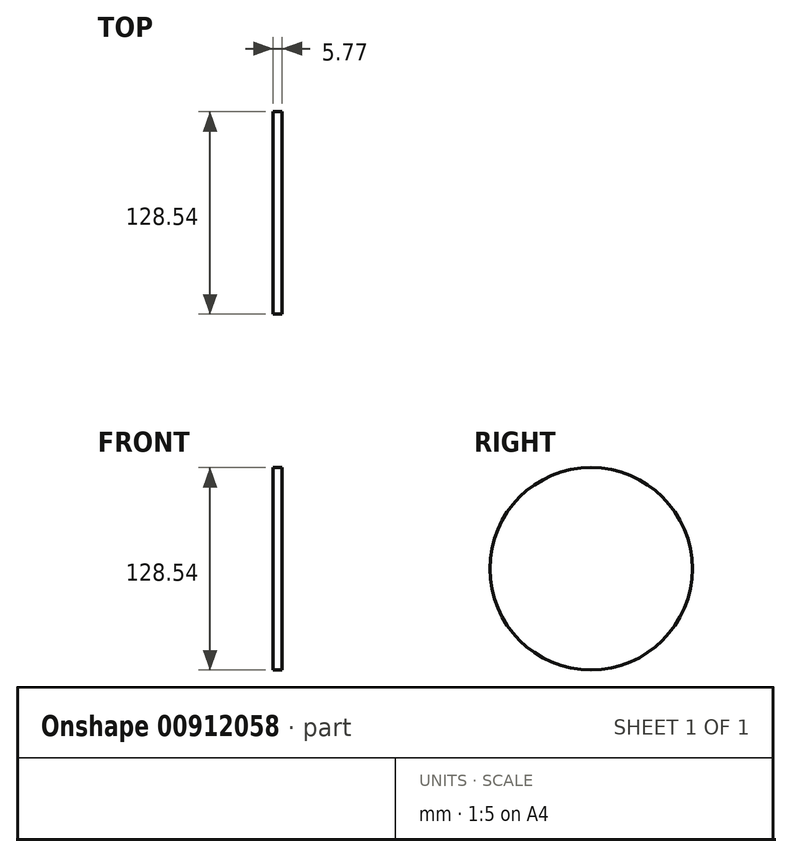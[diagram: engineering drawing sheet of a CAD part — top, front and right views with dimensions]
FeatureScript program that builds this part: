
annotation { "Feature Type Name" : "Feature", "Feature Type Description" : "" }
export const myFeature = defineFeature(function(context is Context, id is Id, definition is map)
    precondition{}
    {
        {
            var Q0;
            Q0=qCreatedBy(makeId("Right.planeOp"),FACE);
            var sketch = newSketch(context, id + "F0", { "sketchPlane" : qUnion([Q0])});
            skLineSegment(sketch, "E0", {"start": v(-7.94, 136.28) * mm, "end": v(-7.94, 136.29) * mm});
            skLineSegment(sketch, "E1.MirrorCS", {"start": v(-7.94, 136.28) * mm, "end": v(-7.94, 136.52) * mm});
            skArc(sketch, "E2.trimOffspring", {"start": v(2.18, 146.92) * mm, "mid": v(-1.44, 143.95) * mm, "end": v(-3.67, 139.84) * mm});
            skPoint(sketch, "E3.start.orphan", {"position": v(0, 68.26) * mm});
            skArc(sketch, "E4.MirrorCS", {"start": v(2.18, 146.92) * mm, "mid": v(5.85, 143.85) * mm, "end": v(8.05, 139.6) * mm});
            skArc(sketch, "E5.MirrorCS", {"start": v(12.63, 135.93) * mm, "mid": v(12.47, 135.94) * mm, "end": v(12.3, 135.96) * mm});
            skArc(sketch, "E6.1.0", {"start": v(-14.9, 146.18) * mm, "mid": v(-10.9, 143.55) * mm, "end": v(-8.21, 139.59) * mm});
            skArc(sketch, "E6.1.1", {"start": v(-14.9, 146.18) * mm, "mid": v(-18.14, 142.81) * mm, "end": v(-19.88, 138.47) * mm});
            skArc(sketch, "E6.1.2", {"start": v(-21.7, 135.42) * mm, "mid": v(-20.52, 136.78) * mm, "end": v(-19.88, 138.47) * mm});
            skArc(sketch, "E6.2.0", {"start": v(-31.76, 143.46) * mm, "mid": v(-27.48, 141.32) * mm, "end": v(-24.36, 137.7) * mm});
            skArc(sketch, "E6.2.1", {"start": v(-31.76, 143.46) * mm, "mid": v(-34.6, 139.74) * mm, "end": v(-35.82, 135.23) * mm});
            skArc(sketch, "E6.2.2", {"start": v(-37.28, 131.99) * mm, "mid": v(-36.26, 133.48) * mm, "end": v(-35.82, 135.23) * mm});
            skArc(sketch, "E6.3.0", {"start": v(-48.2, 138.8) * mm, "mid": v(-43.7, 137.17) * mm, "end": v(-40.18, 133.93) * mm});
            skArc(sketch, "E6.3.1", {"start": v(-48.2, 138.8) * mm, "mid": v(-50.59, 134.78) * mm, "end": v(-51.28, 130.16) * mm});
            skArc(sketch, "E6.3.2", {"start": v(-52.35, 126.77) * mm, "mid": v(-51.5, 128.36) * mm, "end": v(-51.28, 130.16) * mm});
            skArc(sketch, "E6.4.0", {"start": v(-64, 132.27) * mm, "mid": v(-59.33, 131.17) * mm, "end": v(-55.46, 128.36) * mm});
            skArc(sketch, "E6.4.1", {"start": v(-64, 132.27) * mm, "mid": v(-65.9, 128) * mm, "end": v(-66.04, 123.32) * mm});
            skArc(sketch, "E6.4.2", {"start": v(-68.5, 118.08) * mm, "mid": v(-68.43, 118.12) * mm, "end": v(-68.37, 118.16) * mm});
            skArc(sketch, "E6.5.0", {"start": v(-78.91, 123.94) * mm, "mid": v(-74.16, 123.4) * mm, "end": v(-69.99, 121.06) * mm});
            skArc(sketch, "E6.5.1", {"start": v(-78.91, 123.94) * mm, "mid": v(-80.3, 119.48) * mm, "end": v(-79.91, 114.82) * mm});
            skArc(sketch, "E6.5.2", {"start": v(-80.17, 111.28) * mm, "mid": v(-79.72, 113.02) * mm, "end": v(-79.91, 114.82) * mm});
            skArc(sketch, "E6.5.3", {"start": v(-66.71, 119.83) * mm, "mid": v(-68.46, 120.15) * mm, "end": v(-69.99, 121.06) * mm});
            skArc(sketch, "E6.6.0", {"start": v(-92.77, 113.94) * mm, "mid": v(-87.98, 113.95) * mm, "end": v(-83.57, 112.11) * mm});
            skArc(sketch, "E6.6.1", {"start": v(-92.77, 113.94) * mm, "mid": v(-93.64, 109.35) * mm, "end": v(-92.7, 104.77) * mm});
            skArc(sketch, "E6.6.2", {"start": v(-92.55, 101.22) * mm, "mid": v(-92.3, 103) * mm, "end": v(-92.7, 104.77) * mm});
            skArc(sketch, "E6.6.3", {"start": v(-80.17, 111.28) * mm, "mid": v(-81.94, 111.4) * mm, "end": v(-83.57, 112.11) * mm});
            skArc(sketch, "E6.7.0", {"start": v(-105.37, 102.4) * mm, "mid": v(-100.62, 102.97) * mm, "end": v(-96.02, 101.65) * mm});
            skArc(sketch, "E6.7.1", {"start": v(-105.37, 102.4) * mm, "mid": v(-105.7, 97.74) * mm, "end": v(-104.24, 93.3) * mm});
            skArc(sketch, "E6.7.2", {"start": v(-103.68, 89.79) * mm, "mid": v(-103.64, 91.6) * mm, "end": v(-104.24, 93.3) * mm});
            skArc(sketch, "E6.7.3", {"start": v(-92.55, 101.22) * mm, "mid": v(-94.32, 101.13) * mm, "end": v(-96.02, 101.65) * mm});
            skArc(sketch, "E6.8.0", {"start": v(-116.55, 89.48) * mm, "mid": v(-111.9, 90.6) * mm, "end": v(-107.17, 89.82) * mm});
            skArc(sketch, "E6.8.1", {"start": v(-116.55, 89.48) * mm, "mid": v(-116.33, 84.8) * mm, "end": v(-114.36, 80.57) * mm});
            skArc(sketch, "E6.8.2", {"start": v(-113.4, 77.14) * mm, "mid": v(-113.57, 78.94) * mm, "end": v(-114.36, 80.57) * mm});
            skArc(sketch, "E6.8.3", {"start": v(-103.68, 89.79) * mm, "mid": v(-105.43, 89.5) * mm, "end": v(-107.17, 89.82) * mm});
            skArc(sketch, "E6.9.0", {"start": v(-126.15, 75.34) * mm, "mid": v(-121.65, 76.99) * mm, "end": v(-116.87, 76.77) * mm});
            skArc(sketch, "E6.9.1", {"start": v(-126.15, 75.34) * mm, "mid": v(-125.39, 70.73) * mm, "end": v(-122.94, 66.74) * mm});
            skArc(sketch, "E6.9.2", {"start": v(-121.59, 63.46) * mm, "mid": v(-121.97, 65.22) * mm, "end": v(-122.94, 66.74) * mm});
            skArc(sketch, "E6.9.3", {"start": v(-113.4, 77.14) * mm, "mid": v(-115.1, 76.65) * mm, "end": v(-116.87, 76.77) * mm});
            skArc(sketch, "E6.10.0", {"start": v(-134.04, 60.19) * mm, "mid": v(-129.77, 62.34) * mm, "end": v(-125, 62.68) * mm});
            skArc(sketch, "E6.10.1", {"start": v(-134.04, 60.19) * mm, "mid": v(-132.75, 55.7) * mm, "end": v(-129.86, 52.02) * mm});
            skArc(sketch, "E6.10.2", {"start": v(-128.13, 48.91) * mm, "mid": v(-128.72, 50.62) * mm, "end": v(-129.86, 52.02) * mm});
            skArc(sketch, "E6.10.3", {"start": v(-121.59, 63.46) * mm, "mid": v(-123.22, 62.77) * mm, "end": v(-125, 62.68) * mm});
            skArc(sketch, "E6.11.0", {"start": v(-140.12, 44.22) * mm, "mid": v(-136.13, 46.86) * mm, "end": v(-131.43, 47.75) * mm});
            skArc(sketch, "E6.11.1", {"start": v(-140.12, 44.22) * mm, "mid": v(-138.32, 39.9) * mm, "end": v(-135.02, 36.6) * mm});
            skArc(sketch, "E6.11.2", {"start": v(-132.94, 33.7) * mm, "mid": v(-133.72, 35.34) * mm, "end": v(-135.02, 36.6) * mm});
            skArc(sketch, "E6.11.3", {"start": v(-128.13, 48.91) * mm, "mid": v(-129.68, 48.04) * mm, "end": v(-131.43, 47.75) * mm});
            skArc(sketch, "E6.12.0", {"start": v(-144.3, 27.65) * mm, "mid": v(-140.65, 30.74) * mm, "end": v(-136.08, 32.17) * mm});
            skArc(sketch, "E6.12.1", {"start": v(-144.3, 27.65) * mm, "mid": v(-142.02, 23.58) * mm, "end": v(-138.36, 20.67) * mm});
            skArc(sketch, "E6.12.2", {"start": v(-135.96, 18.04) * mm, "mid": v(-136.92, 19.57) * mm, "end": v(-138.36, 20.67) * mm});
            skArc(sketch, "E6.12.3", {"start": v(-132.94, 33.7) * mm, "mid": v(-134.38, 32.66) * mm, "end": v(-136.08, 32.17) * mm});
            skArc(sketch, "E6.13.0", {"start": v(-146.54, 10.71) * mm, "mid": v(-143.26, 14.2) * mm, "end": v(-138.9, 16.15) * mm});
            skArc(sketch, "E6.13.1", {"start": v(-146.54, 10.71) * mm, "mid": v(-143.8, 6.93) * mm, "end": v(-139.82, 4.47) * mm});
            skArc(sketch, "E6.13.2", {"start": v(-137.13, 2.14) * mm, "mid": v(-138.27, 3.55) * mm, "end": v(-139.82, 4.47) * mm});
            skArc(sketch, "E6.13.3", {"start": v(-135.96, 18.04) * mm, "mid": v(-137.26, 16.84) * mm, "end": v(-138.9, 16.15) * mm});
            skArc(sketch, "E6.14.0", {"start": v(-146.8, -6.37) * mm, "mid": v(-143.94, -2.53) * mm, "end": v(-139.83, -0.08) * mm});
            skArc(sketch, "E6.14.1", {"start": v(-146.8, -6.37) * mm, "mid": v(-143.63, -9.8) * mm, "end": v(-139.4, -11.8) * mm});
            skArc(sketch, "E6.14.2", {"start": v(-136.45, -13.8) * mm, "mid": v(-137.74, -12.53) * mm, "end": v(-139.4, -11.8) * mm});
            skArc(sketch, "E6.14.3", {"start": v(-137.13, 2.14) * mm, "mid": v(-138.28, 0.79) * mm, "end": v(-139.83, -0.08) * mm});
            skArc(sketch, "E6.15.0", {"start": v(-145.06, -23.37) * mm, "mid": v(-142.68, -19.22) * mm, "end": v(-138.88, -16.31) * mm});
            skArc(sketch, "E6.15.1", {"start": v(-145.06, -23.37) * mm, "mid": v(-141.52, -26.42) * mm, "end": v(-137.08, -27.9) * mm});
            skArc(sketch, "E6.15.2", {"start": v(-133.93, -29.54) * mm, "mid": v(-135.36, -28.44) * mm, "end": v(-137.08, -27.9) * mm});
            skArc(sketch, "E6.15.3", {"start": v(-136.45, -13.8) * mm, "mid": v(-137.44, -15.27) * mm, "end": v(-138.88, -16.31) * mm});
            skArc(sketch, "E6.16.0", {"start": v(-141.37, -40.05) * mm, "mid": v(-139.48, -35.65) * mm, "end": v(-136.04, -32.33) * mm});
            skArc(sketch, "E6.16.1", {"start": v(-141.37, -40.05) * mm, "mid": v(-137.5, -42.67) * mm, "end": v(-132.92, -43.62) * mm});
            skArc(sketch, "E6.16.2", {"start": v(-129.6, -44.9) * mm, "mid": v(-131.14, -43.96) * mm, "end": v(-132.92, -43.62) * mm});
            skArc(sketch, "E6.16.3", {"start": v(-133.93, -29.54) * mm, "mid": v(-134.74, -31.12) * mm, "end": v(-136.04, -32.33) * mm});
            skArc(sketch, "E6.17.0", {"start": v(-135.76, -56.2) * mm, "mid": v(-134.4, -51.6) * mm, "end": v(-131.37, -47.9) * mm});
            skArc(sketch, "E6.17.1", {"start": v(-135.76, -56.2) * mm, "mid": v(-131.61, -58.34) * mm, "end": v(-126.95, -58.76) * mm});
            skArc(sketch, "E6.17.2", {"start": v(-123.5, -59.63) * mm, "mid": v(-125.15, -58.89) * mm, "end": v(-126.95, -58.76) * mm});
            skArc(sketch, "E6.17.3", {"start": v(-129.6, -44.9) * mm, "mid": v(-130.22, -46.55) * mm, "end": v(-131.37, -47.9) * mm});
            skArc(sketch, "E6.18.0", {"start": v(-128.32, -71.57) * mm, "mid": v(-127.5, -66.86) * mm, "end": v(-124.92, -62.83) * mm});
            skArc(sketch, "E6.18.1", {"start": v(-128.32, -71.57) * mm, "mid": v(-123.95, -73.23) * mm, "end": v(-119.27, -73.1) * mm});
            skArc(sketch, "E6.18.2", {"start": v(-115.75, -73.57) * mm, "mid": v(-117.47, -73.02) * mm, "end": v(-119.27, -73.1) * mm});
            skArc(sketch, "E6.18.3", {"start": v(-123.5, -59.63) * mm, "mid": v(-123.93, -61.36) * mm, "end": v(-124.92, -62.83) * mm});
            skArc(sketch, "E6.19.0", {"start": v(-119.14, -85.99) * mm, "mid": v(-118.88, -81.2) * mm, "end": v(-116.78, -76.9) * mm});
            skArc(sketch, "E6.19.1", {"start": v(-119.14, -85.99) * mm, "mid": v(-114.6, -87.12) * mm, "end": v(-109.98, -86.45) * mm});
            skArc(sketch, "E6.19.2", {"start": v(-106.43, -86.5) * mm, "mid": v(-108.2, -86.16) * mm, "end": v(-109.98, -86.45) * mm});
            skArc(sketch, "E6.19.3", {"start": v(-115.75, -73.57) * mm, "mid": v(-115.97, -75.33) * mm, "end": v(-116.78, -76.9) * mm});
            skArc(sketch, "E6.20.0", {"start": v(-108.36, -99.24) * mm, "mid": v(-108.64, -94.46) * mm, "end": v(-107.06, -89.94) * mm});
            skArc(sketch, "E6.20.1", {"start": v(-108.36, -99.24) * mm, "mid": v(-103.72, -99.84) * mm, "end": v(-99.2, -98.64) * mm});
            skArc(sketch, "E6.20.2", {"start": v(-95.66, -98.28) * mm, "mid": v(-97.46, -98.14) * mm, "end": v(-99.2, -98.64) * mm});
            skArc(sketch, "E6.20.3", {"start": v(-106.43, -86.5) * mm, "mid": v(-106.44, -88.28) * mm, "end": v(-107.06, -89.94) * mm});
            skArc(sketch, "E6.21.0", {"start": v(-96.1, -111.15) * mm, "mid": v(-96.94, -106.43) * mm, "end": v(-95.9, -101.77) * mm});
            skArc(sketch, "E6.21.1", {"start": v(-96.1, -111.15) * mm, "mid": v(-91.43, -111.2) * mm, "end": v(-87.08, -109.49) * mm});
            skArc(sketch, "E6.21.2", {"start": v(-83.6, -108.72) * mm, "mid": v(-85.41, -108.79) * mm, "end": v(-87.08, -109.49) * mm});
            skArc(sketch, "E6.21.3", {"start": v(-95.66, -98.28) * mm, "mid": v(-95.47, -100.04) * mm, "end": v(-95.9, -101.77) * mm});
            skArc(sketch, "E6.22.0", {"start": v(-82.55, -121.55) * mm, "mid": v(-83.93, -116.97) * mm, "end": v(-83.44, -112.21) * mm});
            skArc(sketch, "E6.22.1", {"start": v(-82.55, -121.55) * mm, "mid": v(-77.9, -121.06) * mm, "end": v(-73.78, -118.86) * mm});
            skArc(sketch, "E6.22.2", {"start": v(-70.42, -117.7) * mm, "mid": v(-72.2, -117.97) * mm, "end": v(-73.78, -118.86) * mm});
            skArc(sketch, "E6.22.3", {"start": v(-83.6, -108.72) * mm, "mid": v(-83.21, -110.45) * mm, "end": v(-83.44, -112.21) * mm});
            skArc(sketch, "E6.23.0", {"start": v(-67.88, -130.31) * mm, "mid": v(-69.78, -125.92) * mm, "end": v(-69.84, -121.14) * mm});
            skArc(sketch, "E6.23.1", {"start": v(-67.88, -130.31) * mm, "mid": v(-63.32, -129.29) * mm, "end": v(-59.48, -126.62) * mm});
            skArc(sketch, "E6.23.2", {"start": v(-56.28, -125.07) * mm, "mid": v(-58.02, -125.55) * mm, "end": v(-59.48, -126.62) * mm});
            skArc(sketch, "E6.23.3", {"start": v(-70.42, -117.7) * mm, "mid": v(-69.83, -119.36) * mm, "end": v(-69.84, -121.14) * mm});
            skArc(sketch, "E6.24.0", {"start": v(-52.3, -137.31) * mm, "mid": v(-54.7, -133.17) * mm, "end": v(-55.3, -128.43) * mm});
            skArc(sketch, "E6.24.1", {"start": v(-52.3, -137.31) * mm, "mid": v(-47.88, -135.77) * mm, "end": v(-44.38, -132.67) * mm});
            skArc(sketch, "E6.24.2", {"start": v(-41.38, -130.76) * mm, "mid": v(-43.05, -131.44) * mm, "end": v(-44.38, -132.67) * mm});
            skArc(sketch, "E6.24.3", {"start": v(-56.28, -125.07) * mm, "mid": v(-55.5, -126.66) * mm, "end": v(-55.3, -128.43) * mm});
            skArc(sketch, "E6.25.0", {"start": v(-36, -142.45) * mm, "mid": v(-38.86, -138.62) * mm, "end": v(-40.03, -133.98) * mm});
            skArc(sketch, "E6.25.1", {"start": v(-36, -142.45) * mm, "mid": v(-31.8, -140.4) * mm, "end": v(-28.68, -136.92) * mm});
            skArc(sketch, "E6.25.2", {"start": v(-25.92, -134.68) * mm, "mid": v(-27.5, -135.55) * mm, "end": v(-28.68, -136.92) * mm});
            skArc(sketch, "E6.25.3", {"start": v(-41.38, -130.76) * mm, "mid": v(-40.42, -132.25) * mm, "end": v(-40.03, -133.98) * mm});
            skArc(sketch, "E6.26.0", {"start": v(-19.22, -145.67) * mm, "mid": v(-22.5, -142.2) * mm, "end": v(-24.2, -137.72) * mm});
            skArc(sketch, "E6.26.1", {"start": v(-19.22, -145.67) * mm, "mid": v(-15.28, -143.15) * mm, "end": v(-12.59, -139.33) * mm});
            skArc(sketch, "E6.26.2", {"start": v(-10.1, -136.78) * mm, "mid": v(-11.58, -137.83) * mm, "end": v(-12.59, -139.33) * mm});
            skArc(sketch, "E6.26.3", {"start": v(-25.92, -134.68) * mm, "mid": v(-24.8, -136.05) * mm, "end": v(-24.2, -137.72) * mm});
            skArc(sketch, "E6.27.0", {"start": v(-2.18, -146.92) * mm, "mid": v(-5.85, -143.85) * mm, "end": v(-8.05, -139.6) * mm});
            skArc(sketch, "E6.27.1", {"start": v(-2.18, -146.92) * mm, "mid": v(1.44, -143.95) * mm, "end": v(3.67, -139.84) * mm});
            skArc(sketch, "E6.27.2", {"start": v(5.84, -137.03) * mm, "mid": v(4.5, -138.24) * mm, "end": v(3.67, -139.84) * mm});
            skArc(sketch, "E6.27.3", {"start": v(-10.1, -136.78) * mm, "mid": v(-8.83, -138) * mm, "end": v(-8.05, -139.6) * mm});
            skArc(sketch, "E6.28.0", {"start": v(14.9, -146.18) * mm, "mid": v(10.9, -143.55) * mm, "end": v(8.21, -139.59) * mm});
            skArc(sketch, "E6.28.1", {"start": v(14.9, -146.18) * mm, "mid": v(18.14, -142.81) * mm, "end": v(19.88, -138.47) * mm});
            skArc(sketch, "E6.28.2", {"start": v(21.7, -135.42) * mm, "mid": v(20.52, -136.78) * mm, "end": v(19.88, -138.47) * mm});
            skArc(sketch, "E6.28.3", {"start": v(5.84, -137.03) * mm, "mid": v(7.25, -138.1) * mm, "end": v(8.21, -139.59) * mm});
            skArc(sketch, "E6.29.0", {"start": v(31.76, -143.46) * mm, "mid": v(27.48, -141.32) * mm, "end": v(24.36, -137.7) * mm});
            skArc(sketch, "E6.29.1", {"start": v(31.76, -143.46) * mm, "mid": v(34.6, -139.74) * mm, "end": v(35.82, -135.23) * mm});
            skArc(sketch, "E6.29.2", {"start": v(37.28, -131.99) * mm, "mid": v(36.26, -133.48) * mm, "end": v(35.82, -135.23) * mm});
            skArc(sketch, "E6.29.3", {"start": v(21.7, -135.42) * mm, "mid": v(23.24, -136.32) * mm, "end": v(24.36, -137.7) * mm});
            skArc(sketch, "E6.30.0", {"start": v(48.2, -138.8) * mm, "mid": v(43.7, -137.17) * mm, "end": v(40.18, -133.93) * mm});
            skArc(sketch, "E6.30.1", {"start": v(48.2, -138.8) * mm, "mid": v(50.59, -134.78) * mm, "end": v(51.28, -130.16) * mm});
            skArc(sketch, "E6.30.2", {"start": v(52.35, -126.77) * mm, "mid": v(51.5, -128.36) * mm, "end": v(51.28, -130.16) * mm});
            skArc(sketch, "E6.30.3", {"start": v(37.28, -131.99) * mm, "mid": v(38.9, -132.7) * mm, "end": v(40.18, -133.93) * mm});
            skArc(sketch, "E6.31.0", {"start": v(64, -132.27) * mm, "mid": v(59.33, -131.17) * mm, "end": v(55.46, -128.36) * mm});
            skArc(sketch, "E6.31.1", {"start": v(64, -132.27) * mm, "mid": v(65.9, -128) * mm, "end": v(66.04, -123.32) * mm});
            skArc(sketch, "E6.31.2", {"start": v(66.71, -119.83) * mm, "mid": v(66.06, -121.52) * mm, "end": v(66.04, -123.32) * mm});
            skArc(sketch, "E6.31.3", {"start": v(52.35, -126.77) * mm, "mid": v(54.05, -127.29) * mm, "end": v(55.46, -128.36) * mm});
            skArc(sketch, "E6.32.0", {"start": v(78.91, -123.94) * mm, "mid": v(74.16, -123.4) * mm, "end": v(69.99, -121.06) * mm});
            skArc(sketch, "E6.32.1", {"start": v(78.91, -123.94) * mm, "mid": v(80.3, -119.48) * mm, "end": v(79.91, -114.82) * mm});
            skArc(sketch, "E6.32.2", {"start": v(80.17, -111.28) * mm, "mid": v(79.72, -113.02) * mm, "end": v(79.91, -114.82) * mm});
            skArc(sketch, "E6.32.3", {"start": v(66.71, -119.83) * mm, "mid": v(68.46, -120.15) * mm, "end": v(69.99, -121.06) * mm});
            skArc(sketch, "E6.33.0", {"start": v(92.77, -113.94) * mm, "mid": v(87.98, -113.95) * mm, "end": v(83.57, -112.11) * mm});
            skArc(sketch, "E6.33.1", {"start": v(92.77, -113.94) * mm, "mid": v(93.64, -109.35) * mm, "end": v(92.7, -104.77) * mm});
            skArc(sketch, "E6.33.2", {"start": v(92.55, -101.22) * mm, "mid": v(92.3, -103) * mm, "end": v(92.7, -104.77) * mm});
            skArc(sketch, "E6.33.3", {"start": v(80.17, -111.28) * mm, "mid": v(81.94, -111.4) * mm, "end": v(83.57, -112.11) * mm});
            skArc(sketch, "E6.34.0", {"start": v(105.37, -102.4) * mm, "mid": v(100.62, -102.97) * mm, "end": v(96.02, -101.65) * mm});
            skArc(sketch, "E6.34.1", {"start": v(105.37, -102.4) * mm, "mid": v(105.7, -97.74) * mm, "end": v(104.24, -93.3) * mm});
            skArc(sketch, "E6.34.2", {"start": v(103.68, -89.79) * mm, "mid": v(103.64, -91.6) * mm, "end": v(104.24, -93.3) * mm});
            skArc(sketch, "E6.34.3", {"start": v(92.55, -101.22) * mm, "mid": v(94.32, -101.13) * mm, "end": v(96.02, -101.65) * mm});
            skArc(sketch, "E6.35.0", {"start": v(116.55, -89.48) * mm, "mid": v(111.9, -90.6) * mm, "end": v(107.17, -89.82) * mm});
            skArc(sketch, "E6.35.1", {"start": v(116.55, -89.48) * mm, "mid": v(116.33, -84.8) * mm, "end": v(114.36, -80.57) * mm});
            skArc(sketch, "E6.35.2", {"start": v(113.4, -77.14) * mm, "mid": v(113.57, -78.94) * mm, "end": v(114.36, -80.57) * mm});
            skArc(sketch, "E6.35.3", {"start": v(103.68, -89.79) * mm, "mid": v(105.43, -89.5) * mm, "end": v(107.17, -89.82) * mm});
            skArc(sketch, "E6.36.0", {"start": v(126.15, -75.34) * mm, "mid": v(121.65, -76.99) * mm, "end": v(116.87, -76.77) * mm});
            skArc(sketch, "E6.36.1", {"start": v(126.15, -75.34) * mm, "mid": v(125.39, -70.73) * mm, "end": v(122.94, -66.74) * mm});
            skArc(sketch, "E6.36.2", {"start": v(121.59, -63.46) * mm, "mid": v(121.97, -65.22) * mm, "end": v(122.94, -66.74) * mm});
            skArc(sketch, "E6.36.3", {"start": v(111.4, -78.9) * mm, "mid": v(111.5, -78.77) * mm, "end": v(111.59, -78.64) * mm});
            skArc(sketch, "E6.37.0", {"start": v(134.04, -60.19) * mm, "mid": v(129.77, -62.34) * mm, "end": v(125, -62.68) * mm});
            skArc(sketch, "E6.37.1", {"start": v(134.04, -60.19) * mm, "mid": v(132.75, -55.7) * mm, "end": v(129.86, -52.02) * mm});
            skArc(sketch, "E6.37.2", {"start": v(128.13, -48.91) * mm, "mid": v(128.72, -50.62) * mm, "end": v(129.86, -52.02) * mm});
            skArc(sketch, "E6.37.3", {"start": v(119.81, -65.43) * mm, "mid": v(119.89, -65.3) * mm, "end": v(119.96, -65.15) * mm});
            skArc(sketch, "E6.38.0", {"start": v(140.12, -44.22) * mm, "mid": v(136.13, -46.86) * mm, "end": v(131.43, -47.75) * mm});
            skArc(sketch, "E6.38.1", {"start": v(140.12, -44.22) * mm, "mid": v(138.32, -39.9) * mm, "end": v(135.02, -36.6) * mm});
            skArc(sketch, "E6.38.2", {"start": v(132.94, -33.7) * mm, "mid": v(133.72, -35.34) * mm, "end": v(135.02, -36.6) * mm});
            skArc(sketch, "E6.38.3", {"start": v(126.6, -51.08) * mm, "mid": v(126.66, -50.93) * mm, "end": v(126.72, -50.79) * mm});
            skArc(sketch, "E6.39.0", {"start": v(144.3, -27.65) * mm, "mid": v(140.65, -30.74) * mm, "end": v(136.08, -32.17) * mm});
            skArc(sketch, "E6.39.1", {"start": v(144.3, -27.65) * mm, "mid": v(142.02, -23.58) * mm, "end": v(138.36, -20.67) * mm});
            skArc(sketch, "E6.39.3", {"start": v(131.67, -36.04) * mm, "mid": v(131.71, -35.88) * mm, "end": v(131.76, -35.73) * mm});
            skArc(sketch, "E6.40.0", {"start": v(146.54, -10.71) * mm, "mid": v(143.26, -14.2) * mm, "end": v(138.9, -16.15) * mm});
            skArc(sketch, "E6.40.1", {"start": v(146.54, -10.71) * mm, "mid": v(143.8, -6.93) * mm, "end": v(139.82, -4.47) * mm});
            skArc(sketch, "E6.40.2", {"start": v(137.13, -2.14) * mm, "mid": v(138.27, -3.55) * mm, "end": v(139.82, -4.47) * mm});
            skArc(sketch, "E6.40.3", {"start": v(134.97, -20.5) * mm, "mid": v(134.99, -20.35) * mm, "end": v(135.01, -20.2) * mm});
            skArc(sketch, "E6.41.0", {"start": v(146.8, 6.37) * mm, "mid": v(143.94, 2.53) * mm, "end": v(139.83, 0.08) * mm});
            skArc(sketch, "E6.41.1", {"start": v(146.8, 6.37) * mm, "mid": v(143.63, 9.8) * mm, "end": v(139.4, 11.8) * mm});
            skArc(sketch, "E6.41.2", {"start": v(136.45, 13.8) * mm, "mid": v(137.74, 12.53) * mm, "end": v(139.4, 11.8) * mm});
            skArc(sketch, "E6.41.3", {"start": v(137.13, -2.14) * mm, "mid": v(138.28, -0.79) * mm, "end": v(139.83, 0.08) * mm});
            skArc(sketch, "E6.42.0", {"start": v(145.06, 23.37) * mm, "mid": v(142.68, 19.22) * mm, "end": v(138.88, 16.31) * mm});
            skArc(sketch, "E6.42.1", {"start": v(145.06, 23.37) * mm, "mid": v(141.52, 26.42) * mm, "end": v(137.08, 27.9) * mm});
            skArc(sketch, "E6.42.2", {"start": v(132.77, 31.76) * mm, "mid": v(132.79, 31.68) * mm, "end": v(132.8, 31.6) * mm});
            skArc(sketch, "E6.42.3", {"start": v(136.06, 11.17) * mm, "mid": v(136.04, 11.33) * mm, "end": v(136.03, 11.49) * mm});
            skArc(sketch, "E6.43.0", {"start": v(141.37, 40.05) * mm, "mid": v(139.48, 35.65) * mm, "end": v(136.04, 32.33) * mm});
            skArc(sketch, "E6.43.1", {"start": v(141.37, 40.05) * mm, "mid": v(137.5, 42.67) * mm, "end": v(132.92, 43.62) * mm});
            skArc(sketch, "E6.43.2", {"start": v(129.6, 44.9) * mm, "mid": v(131.14, 43.96) * mm, "end": v(132.92, 43.62) * mm});
            skArc(sketch, "E6.43.3", {"start": v(133.84, 26.9) * mm, "mid": v(133.8, 27.05) * mm, "end": v(133.78, 27.2) * mm});
            skArc(sketch, "E6.44.0", {"start": v(135.76, 56.2) * mm, "mid": v(134.4, 51.6) * mm, "end": v(131.37, 47.9) * mm});
            skArc(sketch, "E6.44.1", {"start": v(135.76, 56.2) * mm, "mid": v(131.61, 58.34) * mm, "end": v(126.95, 58.76) * mm});
            skArc(sketch, "E6.44.2", {"start": v(123.5, 59.63) * mm, "mid": v(125.15, 58.89) * mm, "end": v(126.95, 58.76) * mm});
            skArc(sketch, "E6.44.3", {"start": v(129.81, 42.25) * mm, "mid": v(129.76, 42.4) * mm, "end": v(129.72, 42.55) * mm});
            skArc(sketch, "E6.45.0", {"start": v(128.32, 71.57) * mm, "mid": v(127.5, 66.86) * mm, "end": v(124.92, 62.83) * mm});
            skArc(sketch, "E6.45.1", {"start": v(128.32, 71.57) * mm, "mid": v(123.95, 73.23) * mm, "end": v(119.27, 73.1) * mm});
            skArc(sketch, "E6.45.2", {"start": v(115.75, 73.57) * mm, "mid": v(117.47, 73.02) * mm, "end": v(119.27, 73.1) * mm});
            skArc(sketch, "E6.45.3", {"start": v(124.03, 57.03) * mm, "mid": v(123.96, 57.17) * mm, "end": v(123.9, 57.32) * mm});
            skArc(sketch, "E6.46.0", {"start": v(119.14, 85.99) * mm, "mid": v(118.88, 81.2) * mm, "end": v(116.78, 76.9) * mm});
            skArc(sketch, "E6.46.1", {"start": v(119.14, 85.99) * mm, "mid": v(114.6, 87.12) * mm, "end": v(109.98, 86.45) * mm});
            skArc(sketch, "E6.46.2", {"start": v(106.43, 86.5) * mm, "mid": v(108.2, 86.16) * mm, "end": v(109.98, 86.45) * mm});
            skArc(sketch, "E6.46.3", {"start": v(116.57, 71.04) * mm, "mid": v(116.49, 71.18) * mm, "end": v(116.4, 71.32) * mm});
            skArc(sketch, "E6.47.0", {"start": v(108.36, 99.24) * mm, "mid": v(108.64, 94.46) * mm, "end": v(107.06, 89.94) * mm});
            skArc(sketch, "E6.47.1", {"start": v(108.36, 99.24) * mm, "mid": v(103.72, 99.84) * mm, "end": v(99.2, 98.64) * mm});
            skArc(sketch, "E6.47.3", {"start": v(107.54, 84.1) * mm, "mid": v(107.44, 84.22) * mm, "end": v(107.34, 84.35) * mm});
            skArc(sketch, "E6.48.0", {"start": v(96.1, 111.15) * mm, "mid": v(96.94, 106.43) * mm, "end": v(95.9, 101.77) * mm});
            skArc(sketch, "E6.48.1", {"start": v(96.1, 111.15) * mm, "mid": v(91.43, 111.2) * mm, "end": v(87.08, 109.49) * mm});
            skArc(sketch, "E6.48.2", {"start": v(83.6, 108.72) * mm, "mid": v(85.41, 108.79) * mm, "end": v(87.08, 109.49) * mm});
            skArc(sketch, "E6.48.3", {"start": v(97.05, 96.01) * mm, "mid": v(96.93, 96.12) * mm, "end": v(96.82, 96.24) * mm});
            skArc(sketch, "E6.49.0", {"start": v(82.55, 121.55) * mm, "mid": v(83.93, 116.97) * mm, "end": v(83.44, 112.21) * mm});
            skArc(sketch, "E6.49.1", {"start": v(82.55, 121.55) * mm, "mid": v(77.9, 121.06) * mm, "end": v(73.78, 118.86) * mm});
            skArc(sketch, "E6.49.2", {"start": v(70.42, 117.7) * mm, "mid": v(72.2, 117.97) * mm, "end": v(73.78, 118.86) * mm});
            skArc(sketch, "E6.49.3", {"start": v(85.24, 106.63) * mm, "mid": v(85.12, 106.73) * mm, "end": v(85, 106.83) * mm});
            skArc(sketch, "E6.50.0", {"start": v(67.88, 130.31) * mm, "mid": v(69.78, 125.92) * mm, "end": v(69.84, 121.14) * mm});
            skArc(sketch, "E6.50.1", {"start": v(67.88, 130.31) * mm, "mid": v(63.32, 129.29) * mm, "end": v(59.48, 126.62) * mm});
            skArc(sketch, "E6.50.2", {"start": v(56.28, 125.07) * mm, "mid": v(58.02, 125.55) * mm, "end": v(59.48, 126.62) * mm});
            skArc(sketch, "E6.50.3", {"start": v(72.29, 115.8) * mm, "mid": v(72.15, 115.89) * mm, "end": v(72.02, 115.97) * mm});
            skArc(sketch, "E6.51.0", {"start": v(52.3, 137.31) * mm, "mid": v(54.7, 133.17) * mm, "end": v(55.3, 128.43) * mm});
            skArc(sketch, "E6.51.1", {"start": v(52.3, 137.31) * mm, "mid": v(47.88, 135.77) * mm, "end": v(44.38, 132.67) * mm});
            skArc(sketch, "E6.51.2", {"start": v(41.38, 130.76) * mm, "mid": v(43.05, 131.44) * mm, "end": v(44.38, 132.67) * mm});
            skArc(sketch, "E6.51.3", {"start": v(58.35, 123.41) * mm, "mid": v(58.21, 123.48) * mm, "end": v(58.07, 123.55) * mm});
            skArc(sketch, "E6.52.0", {"start": v(36, 142.45) * mm, "mid": v(38.86, 138.62) * mm, "end": v(40.03, 133.98) * mm});
            skArc(sketch, "E6.52.1", {"start": v(36, 142.45) * mm, "mid": v(31.8, 140.4) * mm, "end": v(28.68, 136.92) * mm});
            skArc(sketch, "E6.52.2", {"start": v(23.43, 134.49) * mm, "mid": v(23.5, 134.47) * mm, "end": v(23.58, 134.46) * mm});
            skArc(sketch, "E6.52.3", {"start": v(41.38, 130.76) * mm, "mid": v(40.42, 132.25) * mm, "end": v(40.03, 133.98) * mm});
            skArc(sketch, "E6.53.0", {"start": v(19.22, 145.67) * mm, "mid": v(22.5, 142.2) * mm, "end": v(24.2, 137.72) * mm});
            skArc(sketch, "E6.53.1", {"start": v(19.22, 145.67) * mm, "mid": v(15.28, 143.15) * mm, "end": v(12.59, 139.33) * mm});
            skArc(sketch, "E6.53.2", {"start": v(7.65, 136.3) * mm, "mid": v(7.73, 136.3) * mm, "end": v(7.81, 136.3) * mm});
            skArc(sketch, "E6.53.3", {"start": v(28.32, 133.55) * mm, "mid": v(28.16, 133.58) * mm, "end": v(28.01, 133.61) * mm});
            skCircle(sketch, "E7", {"center": v(0, 0) * mm, "radius": 64.27 * mm});
            skCircle(sketch, "E8", {"center": v(0, 0) * mm, "radius": 137.15 * mm});
            skArc(sketch, "E9.trimOffspring", {"start": v(-66.71, 119.83) * mm, "mid": v(-66.06, 121.52) * mm, "end": v(-66.04, 123.32) * mm});
            skArc(sketch, "E10.trimOffspring", {"start": v(-52.35, 126.77) * mm, "mid": v(-54.05, 127.29) * mm, "end": v(-55.46, 128.36) * mm});
            skArc(sketch, "E11.trimOffspring", {"start": v(-37.28, 131.99) * mm, "mid": v(-38.9, 132.7) * mm, "end": v(-40.18, 133.93) * mm});
            skArc(sketch, "E12.trimOffspring", {"start": v(-21.7, 135.42) * mm, "mid": v(-23.24, 136.32) * mm, "end": v(-24.36, 137.7) * mm});
            skArc(sketch, "E13.trimOffspring", {"start": v(-7.94, 136.28) * mm, "mid": v(-8, 136.28) * mm, "end": v(-8.06, 136.28) * mm});
            skArc(sketch, "E14.trimOffspring", {"start": v(-5.84, 137.03) * mm, "mid": v(-4.5, 138.24) * mm, "end": v(-3.67, 139.84) * mm});
            skArc(sketch, "E15.trimOffspring", {"start": v(-5.84, 137.03) * mm, "mid": v(-7.25, 138.1) * mm, "end": v(-8.21, 139.59) * mm});
            skArc(sketch, "E16.trimOffspring", {"start": v(-3.24, 136.48) * mm, "mid": v(-3.4, 136.47) * mm, "end": v(-3.56, 136.47) * mm});
            skArc(sketch, "E17.trimOffspring", {"start": v(10.1, 136.78) * mm, "mid": v(11.58, 137.83) * mm, "end": v(12.59, 139.33) * mm});
            skArc(sketch, "E18.trimOffspring", {"start": v(10.1, 136.78) * mm, "mid": v(8.83, 138) * mm, "end": v(8.05, 139.6) * mm});
            skArc(sketch, "E19.trimOffspring", {"start": v(25.92, 134.68) * mm, "mid": v(27.5, 135.55) * mm, "end": v(28.68, 136.92) * mm});
            skArc(sketch, "E20.trimOffspring", {"start": v(25.92, 134.68) * mm, "mid": v(24.8, 136.05) * mm, "end": v(24.2, 137.72) * mm});
            skArc(sketch, "E21.trimOffspring", {"start": v(28.32, 133.55) * mm, "mid": v(28.17, 133.58) * mm, "end": v(28.01, 133.61) * mm});
            skArc(sketch, "E22.trimOffspring", {"start": v(56.28, 125.07) * mm, "mid": v(55.5, 126.66) * mm, "end": v(55.3, 128.43) * mm});
            skArc(sketch, "E23.trimOffspring", {"start": v(70.42, 117.7) * mm, "mid": v(69.83, 119.36) * mm, "end": v(69.84, 121.14) * mm});
            skArc(sketch, "E24.trimOffspring", {"start": v(83.6, 108.72) * mm, "mid": v(83.21, 110.45) * mm, "end": v(83.44, 112.21) * mm});
            skArc(sketch, "E25.trimOffspring", {"start": v(95.66, 98.28) * mm, "mid": v(97.46, 98.14) * mm, "end": v(99.2, 98.64) * mm});
            skArc(sketch, "E26.trimOffspring", {"start": v(95.66, 98.28) * mm, "mid": v(95.47, 100.04) * mm, "end": v(95.9, 101.77) * mm});
            skArc(sketch, "E27.trimOffspring", {"start": v(97.05, 96.01) * mm, "mid": v(96.93, 96.13) * mm, "end": v(96.82, 96.24) * mm});
            skArc(sketch, "E28.trimOffspring", {"start": v(106.43, 86.5) * mm, "mid": v(106.44, 88.28) * mm, "end": v(107.06, 89.94) * mm});
            skArc(sketch, "E29.trimOffspring", {"start": v(115.75, 73.57) * mm, "mid": v(115.97, 75.33) * mm, "end": v(116.78, 76.9) * mm});
            skArc(sketch, "E30.trimOffspring", {"start": v(124.03, 57.03) * mm, "mid": v(123.97, 57.18) * mm, "end": v(123.9, 57.32) * mm});
            skArc(sketch, "E31.trimOffspring", {"start": v(123.5, 59.63) * mm, "mid": v(123.93, 61.36) * mm, "end": v(124.92, 62.83) * mm});
            skArc(sketch, "E32.trimOffspring", {"start": v(129.6, 44.9) * mm, "mid": v(130.22, 46.55) * mm, "end": v(131.37, 47.9) * mm});
            skArc(sketch, "E33.trimOffspring", {"start": v(133.93, 29.54) * mm, "mid": v(135.36, 28.44) * mm, "end": v(137.08, 27.9) * mm});
            skArc(sketch, "E34.trimOffspring", {"start": v(133.93, 29.54) * mm, "mid": v(134.74, 31.12) * mm, "end": v(136.04, 32.33) * mm});
            skArc(sketch, "E35.trimOffspring", {"start": v(136.45, 13.8) * mm, "mid": v(137.44, 15.27) * mm, "end": v(138.88, 16.31) * mm});
            skArc(sketch, "E36.trimOffspring", {"start": v(135.96, -18.04) * mm, "mid": v(136.92, -19.57) * mm, "end": v(138.36, -20.67) * mm});
            skArc(sketch, "E37.trimOffspring", {"start": v(135.96, -18.04) * mm, "mid": v(137.26, -16.84) * mm, "end": v(138.9, -16.15) * mm});
            skArc(sketch, "E38.trimOffspring", {"start": v(132.94, -33.7) * mm, "mid": v(134.38, -32.66) * mm, "end": v(136.08, -32.17) * mm});
            skArc(sketch, "E39.trimOffspring", {"start": v(128.13, -48.91) * mm, "mid": v(129.68, -48.04) * mm, "end": v(131.43, -47.75) * mm});
            skArc(sketch, "E40.trimOffspring", {"start": v(121.59, -63.46) * mm, "mid": v(123.22, -62.77) * mm, "end": v(125, -62.68) * mm});
            skArc(sketch, "E41.trimOffspring", {"start": v(113.4, -77.14) * mm, "mid": v(115.1, -76.65) * mm, "end": v(116.87, -76.77) * mm});
            skArc(sketch, "E42.trimOffspring", {"start": v(-25.62, 151.07) * mm, "mid": v(-22.03, 152.56) * mm, "end": v(-20.54, 156.15) * mm});
            skArc(sketch, "E43.trimOffspring", {"start": v(-17.69, 163.47) * mm, "mid": v(-19.8, 160.08) * mm, "end": v(-20.54, 156.15) * mm});
            skArc(sketch, "E44.MirrorCS", {"start": v(-9.75, 151.07) * mm, "mid": v(-13.34, 152.56) * mm, "end": v(-14.83, 156.15) * mm});
            skArc(sketch, "E45.MirrorCS", {"start": v(-17.69, 163.47) * mm, "mid": v(-15.57, 160.08) * mm, "end": v(-14.83, 156.15) * mm});
            skArc(sketch, "E46.MirrorCS", {"start": v(-9.75, 151.07) * mm, "mid": v(-6.16, 152.56) * mm, "end": v(-4.67, 156.15) * mm});
            skArc(sketch, "E47.MirrorCS", {"start": v(-25.62, 151.07) * mm, "mid": v(-29.22, 152.56) * mm, "end": v(-30.7, 156.15) * mm});
            skSolve(sketch);
        }
        {
            var Q0;
            Q0=sQuery(id+"F0.wireOp",EDGE,"CG3f1oHO-txOG-49Xd-RbCl-f0HtQFe9ZqMT");
            var Q1;
            Q1=sQuery(id+"F0.wireOp",EDGE,"E7");
            extrude(context, id + "F1", {"bodyType" : ToolBodyType.SURFACE, "surfaceEntities" : qUnion([Q0, Q1]), "depth" : 5.77 * mm, "offsetDistance" : 25.4 * mm});
        }
    });
